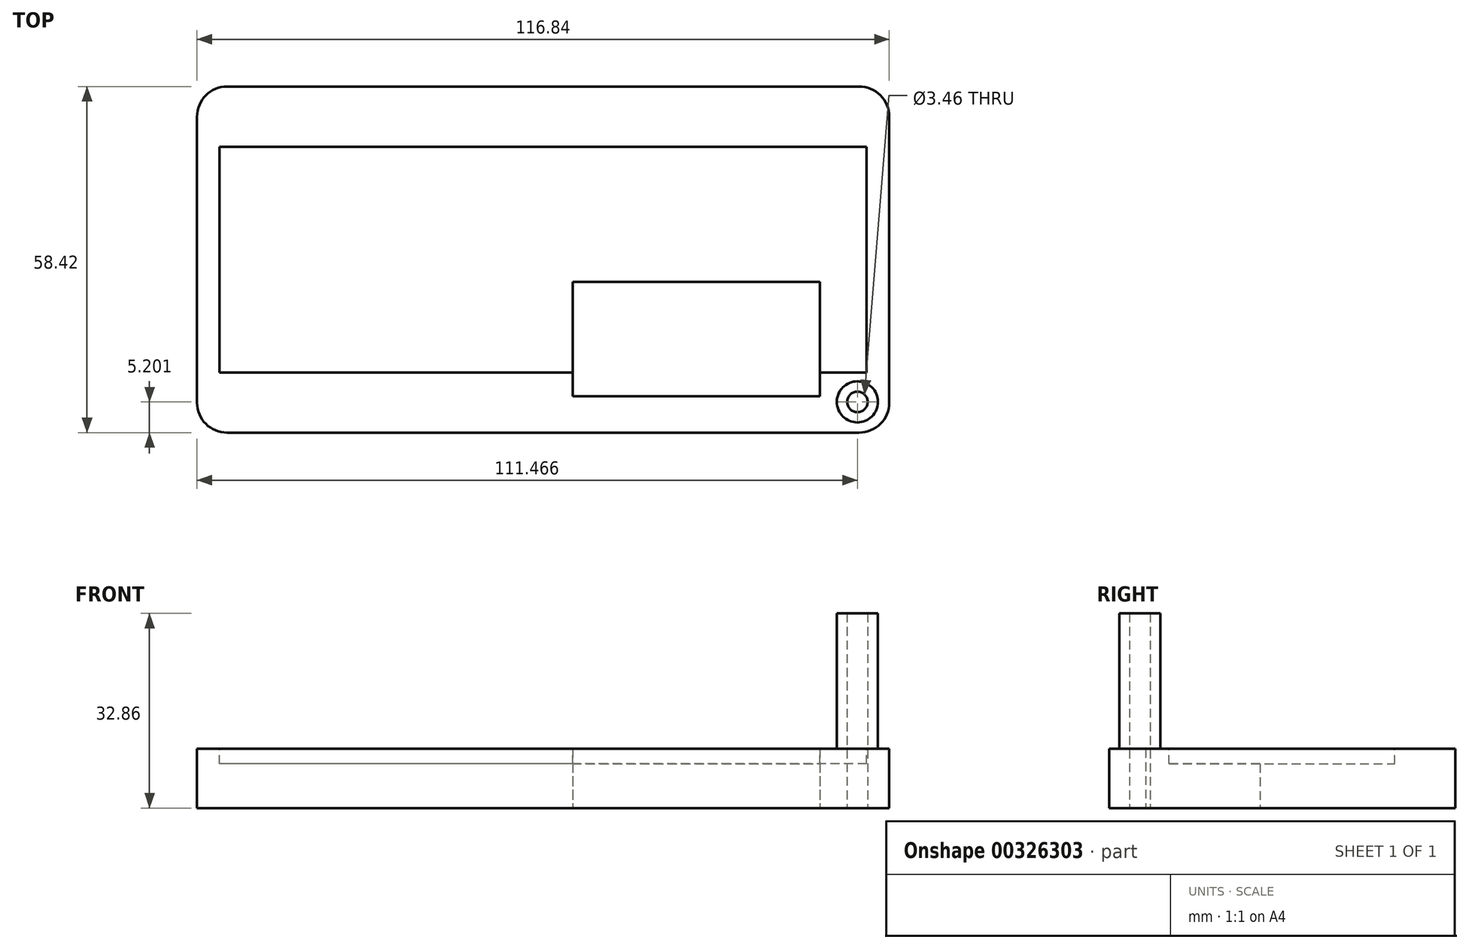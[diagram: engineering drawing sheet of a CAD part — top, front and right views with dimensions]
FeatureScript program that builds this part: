
annotation { "Feature Type Name" : "Feature", "Feature Type Description" : "" }
export const myFeature = defineFeature(function(context is Context, id is Id, definition is map)
    precondition{}
    {
        {
            var Q0;
            Q0=qCreatedBy(makeId("Top.planeOp"),FACE);
            var sketch = newSketch(context, id + "F0", { "sketchPlane" : qUnion([Q0])});
            skLineSegment(sketch, "E0.bottom", {"start": v(58.42, -29.2) * mm, "end": v(-58.42, -29.21) * mm});
            skLineSegment(sketch, "E0.top", {"start": v(58.42, 29.21) * mm, "end": v(-58.42, 29.2) * mm});
            skLineSegment(sketch, "E0.left", {"start": v(58.42, -29.2) * mm, "end": v(58.42, 29.21) * mm});
            skLineSegment(sketch, "E0.right", {"start": v(-58.42, -29.21) * mm, "end": v(-58.42, 29.2) * mm});
            skPoint(sketch, "E0.middle", {"position": v(0, 0) * mm});
            skSolve(sketch);
        }
        {
            var Q0;
            Q0=makeQuery(id+"F0.imprint","IMPRINT",FACE,{"disambiguationData":[TD([[makeQuery(id+"F0.imprint","IMPRINT",EDGE,{"derivedFrom":sQuery(id+"F0.wireOp",EDGE,"E0.bottom")}),-1.0]])]});
            extrude(context, id + "F1", {"entities" : qUnion([Q0]), "depth" : 10 * mm});
        }
        {
            var Q0;
            Q0=makeQuery(id+"F1.opExtrude","CAP_FACE",FACE,{"disambiguationData":[OSD([sQuery(id+"F0.wireOp",EDGE,"E0.bottom"),sQuery(id+"F0.wireOp",EDGE,"E0.top"),sQuery(id+"F0.wireOp",EDGE,"E0.left"),sQuery(id+"F0.wireOp",EDGE,"E0.right")])],"isStart":false});
            var sketch = newSketch(context, id + "F2", { "sketchPlane" : qUnion([Q0])});
            skCircle(sketch, "E1", {"center": v(53.05, -24) * mm, "radius": 3.47 * mm});
            skCircle(sketch, "E2", {"center": v(53.05, -24) * mm, "radius": 1.73 * mm});
            skSolve(sketch);
        }
        {
            var Q0;
            {var subQ0=sQuery(id+"F2.wireOp",EDGE,"XDbaI23f-IPFS-wJkp-U8DP-RhBmWaWZ9qTY.right");var subQ1=sQuery(id+"F2.wireOp",EDGE,"XDbaI23f-IPFS-wJkp-U8DP-RhBmWaWZ9qTY.top");var subQ2=makeQuery(id+"F2.imprint","INTERSECT",VERTEX,{"derivedFrom":[subQ1,subQ0]});Q0=makeQuery(id+"F2.imprint","IMPRINT",FACE,{"disambiguationData":[TD([[makeQuery(id+"F2.imprint","IMPRINT",EDGE,{"disambiguationData":[TD([[subQ2,1.0]])],"derivedFrom":subQ1}),-1.0]])]});}
            var Q1;
            Q1=makeQuery(id+"F2.imprint","IMPRINT",FACE,{"disambiguationData":[TD([[makeQuery(id+"F2.imprint","IMPRINT",EDGE,{"derivedFrom":sQuery(id+"F2.wireOp",EDGE,"E1")}),1.0]])]});
            extrude(context, id + "F3", {"entities" : qUnion([Q0, Q1]), "operationType" : NewBodyOperationType.ADD, "depth" : 22.86 * mm});
        }
        {
            var Q0;
            Q0=makeQuery(id+"F1.opExtrude","SWEPT_EDGE",EDGE,{"disambiguationData":[OSD([sQuery(id+"F0.wireOp",EDGE,"E0.bottom"),sQuery(id+"F0.wireOp",EDGE,"E0.left")])]});
            var Q1;
            Q1=makeQuery(id+"F1.opExtrude","SWEPT_EDGE",EDGE,{"disambiguationData":[OSD([sQuery(id+"F0.wireOp",EDGE,"E0.bottom"),sQuery(id+"F0.wireOp",EDGE,"E0.right")])]});
            var Q2;
            Q2=makeQuery(id+"F1.opExtrude","SWEPT_EDGE",EDGE,{"disambiguationData":[OSD([sQuery(id+"F0.wireOp",EDGE,"E0.top"),sQuery(id+"F0.wireOp",EDGE,"E0.left")])]});
            var Q3;
            Q3=makeQuery(id+"F1.opExtrude","SWEPT_EDGE",EDGE,{"disambiguationData":[OSD([sQuery(id+"F0.wireOp",EDGE,"E0.top"),sQuery(id+"F0.wireOp",EDGE,"E0.right")])]});
            fillet(context, id + "F4", {"entities" : qUnion([Q0, Q1, Q2, Q3]), "radius" : 5.08 * mm, "tangentPropagation" : true, "allowEdgeOverflow" : false});
        }
        {
            var Q0;
            Q0=makeQuery(id+"F3.boolean.opBoolean","SPLIT",FACE,{"disambiguationData":[TD([makeQuery(id+"F3.opExtrude","SWEPT_FACE",FACE,{"disambiguationData":[OSD([sQuery(id+"F2.wireOp",EDGE,"E2")])]})])],"derivedFrom":makeQuery(id+"F1.opExtrude","CAP_FACE",FACE,{"disambiguationData":[OSD([sQuery(id+"F0.wireOp",EDGE,"E0.bottom"),sQuery(id+"F0.wireOp",EDGE,"E0.top"),sQuery(id+"F0.wireOp",EDGE,"E0.left"),sQuery(id+"F0.wireOp",EDGE,"E0.right")])],"isStart":false})});
            var sketch = newSketch(context, id + "F5", { "sketchPlane" : qUnion([Q0])});
            skCircle(sketch, "E3", {"center": v(53.05, -24) * mm, "radius": 1.73 * mm});
            skSolve(sketch);
        }
        {
            var Q0;
            Q0 = qSketchRegion(id + "F5", true);
            extrude(context, id + "F6", {"entities" : qUnion([Q0]), "operationType" : NewBodyOperationType.REMOVE, "oppositeDirection" : true, "depth" : 21.59 * mm});
        }
        {
            var Q0;
            Q0=qCreatedBy(makeId("Top.planeOp"),FACE);
            var sketch = newSketch(context, id + "F7", { "sketchPlane" : qUnion([Q0])});
            skLineSegment(sketch, "E4.bottom", {"start": v(4.98, -3.74) * mm, "end": v(46.7, -3.74) * mm});
            skLineSegment(sketch, "E4.top", {"start": v(4.98, -23.04) * mm, "end": v(46.7, -23.04) * mm});
            skLineSegment(sketch, "E4.left", {"start": v(4.98, -3.74) * mm, "end": v(4.98, -23.04) * mm});
            skLineSegment(sketch, "E4.right", {"start": v(46.7, -3.74) * mm, "end": v(46.7, -23.04) * mm});
            skSolve(sketch);
        }
        {
            var Q0;
            Q0 = qSketchRegion(id + "F7", true);
            extrude(context, id + "F8", {"entities" : qUnion([Q0]), "operationType" : NewBodyOperationType.REMOVE, "depth" : 53.1 * mm});
        }
        {
            var Q0;
            Q0=makeQuery(id+"F2.imprint","IMPRINT",FACE,{"disambiguationData":[TD([[makeQuery(id+"F2.imprint","IMPRINT",EDGE,{"derivedFrom":sQuery(id+"F2.wireOp",EDGE,"E1")}),-1.0]])]});
            var sketch = newSketch(context, id + "F9", { "sketchPlane" : qUnion([Q0])});
            skLineSegment(sketch, "E5.bottom", {"start": v(54.61, -19.05) * mm, "end": v(-54.61, -19.05) * mm});
            skLineSegment(sketch, "E5.top", {"start": v(54.61, 19.05) * mm, "end": v(-54.61, 19.05) * mm});
            skLineSegment(sketch, "E5.left", {"start": v(54.61, -19.05) * mm, "end": v(54.61, 19.05) * mm});
            skLineSegment(sketch, "E5.right", {"start": v(-54.61, -19.05) * mm, "end": v(-54.61, 19.05) * mm});
            skPoint(sketch, "E5.middle", {"position": v(0, 0) * mm});
            skSolve(sketch);
        }
        {
            var Q0;
            Q0 = qSketchRegion(id + "F9", true);
            extrude(context, id + "F10", {"entities" : qUnion([Q0]), "operationType" : NewBodyOperationType.REMOVE, "oppositeDirection" : true, "depth" : 2.54 * mm});
        }
    });
